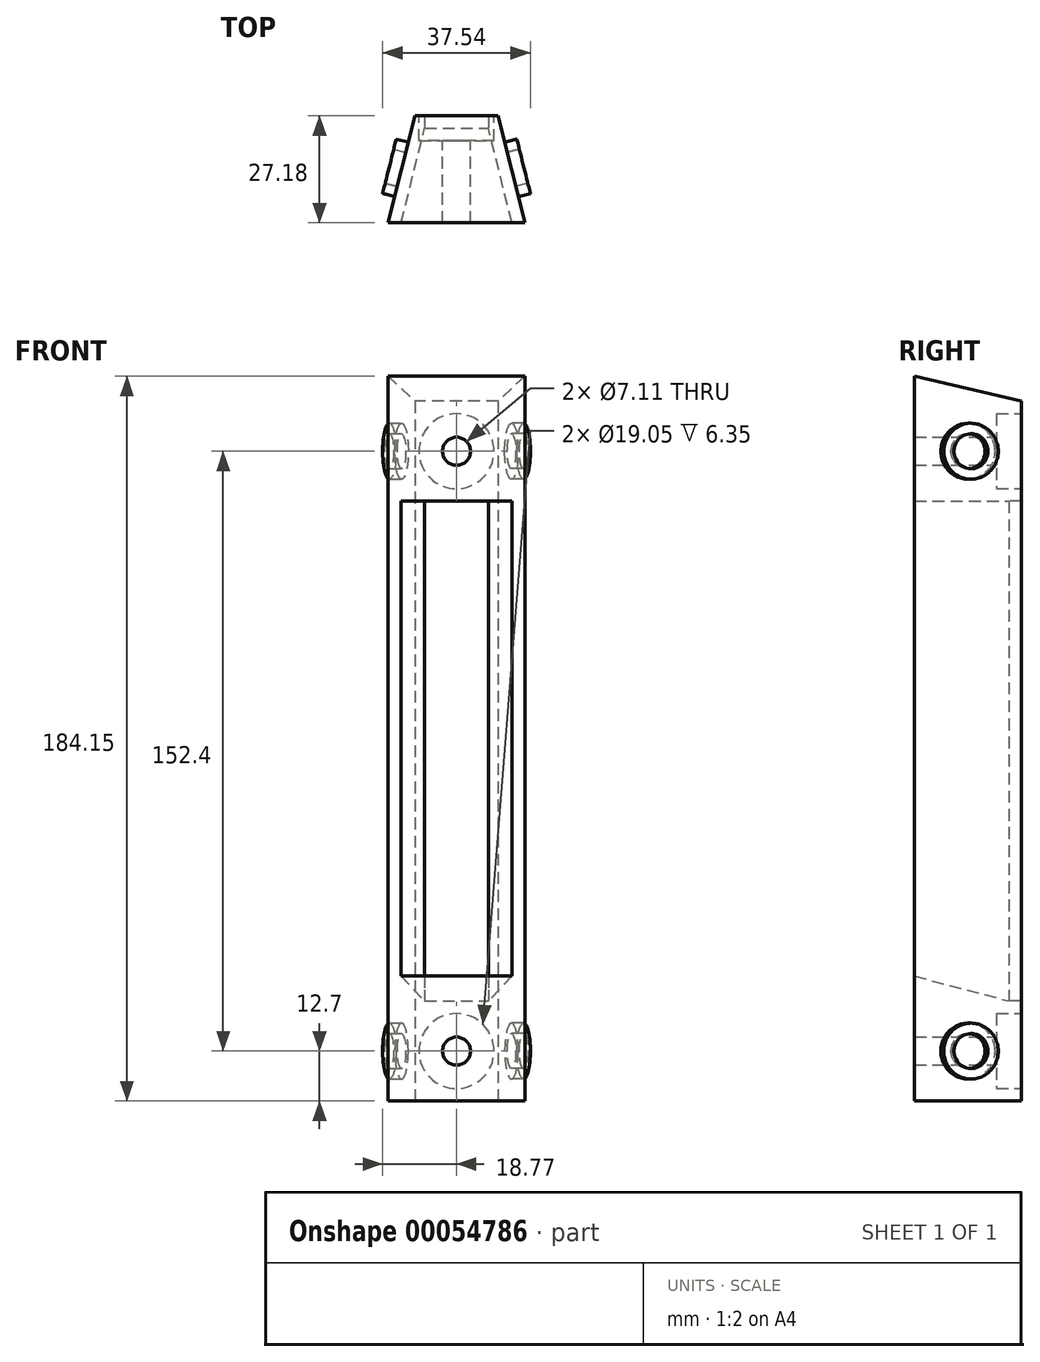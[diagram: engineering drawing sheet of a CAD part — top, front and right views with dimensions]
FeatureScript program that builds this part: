
annotation { "Feature Type Name" : "Feature", "Feature Type Description" : "" }
export const myFeature = defineFeature(function(context is Context, id is Id, definition is map)
    precondition{}
    {
        {
            var Q0;
            Q0=qCreatedBy(makeId("Top.planeOp"),FACE);
            var sketch = newSketch(context, id + "F0", { "sketchPlane" : qUnion([Q0])});
            skLineSegment(sketch, "E0", {"start": v(-39.69, 0) * mm, "end": v(-20.64, 0) * mm});
            skLineSegment(sketch, "E1", {"start": v(-20.64, 0) * mm, "end": v(-13.3, 29.35) * mm});
            skLineSegment(sketch, "E2", {"start": v(-10.22, 31.75) * mm, "end": v(10.22, 31.75) * mm});
            skLineSegment(sketch, "E3", {"start": v(13.3, 29.35) * mm, "end": v(20.64, 0) * mm});
            skLineSegment(sketch, "E4", {"start": v(20.64, 0) * mm, "end": v(39.69, 0) * mm});
            skLineSegment(sketch, "E5", {"start": v(0, 0) * mm, "end": v(0, 38.89) * mm, "construction": true});
            skPoint(sketch, "E6.visualSharp", {"position": v(-12.7, 31.75) * mm});
            skArc(sketch, "E6.filletArc", {"start": v(-10.22, 31.75) * mm, "mid": v(-12.17, 31.08) * mm, "end": v(-13.3, 29.35) * mm});
            skPoint(sketch, "E7.visualSharp", {"position": v(12.7, 31.75) * mm});
            skArc(sketch, "E7.filletArc", {"start": v(13.3, 29.35) * mm, "mid": v(12.17, 31.08) * mm, "end": v(10.22, 31.75) * mm});
            skLineSegment(sketch, "E8", {"start": v(-17.36, 0) * mm, "end": v(-14.1, 0) * mm});
            skLineSegment(sketch, "E9", {"start": v(-14.1, 0) * mm, "end": v(-8.1, 24) * mm});
            skLineSegment(sketch, "E10", {"start": v(-8.1, 24) * mm, "end": v(8.1, 24) * mm});
            skLineSegment(sketch, "E11", {"start": v(8.1, 24) * mm, "end": v(14.1, 0) * mm});
            skLineSegment(sketch, "E12", {"start": v(14.1, 0) * mm, "end": v(17.36, 0) * mm});
            skLineSegment(sketch, "E13", {"start": v(17.36, 0) * mm, "end": v(10.57, 27.18) * mm});
            skLineSegment(sketch, "E14", {"start": v(10.57, 27.18) * mm, "end": v(-10.57, 27.18) * mm});
            skLineSegment(sketch, "E15", {"start": v(-10.57, 27.18) * mm, "end": v(-17.36, 0) * mm});
            skSolve(sketch);
        }
        {
            var Q0;
            Q0=makeQuery(id+"F0.imprint","IMPRINT",FACE,{"disambiguationData":[TD([[makeQuery(id+"F0.imprint","IMPRINT",EDGE,{"derivedFrom":sQuery(id+"F0.wireOp",EDGE,"E8")}),1.0]])]});
            extrude(context, id + "F1", {"entities" : qUnion([Q0]), "depth" : 127 * mm});
        }
        {
            var Q0;
            Q0=makeQuery(id+"F1.opExtrude","CAP_FACE",FACE,{"disambiguationData":[OSD([sQuery(id+"F0.wireOp",EDGE,"E8"),sQuery(id+"F0.wireOp",EDGE,"E9"),sQuery(id+"F0.wireOp",EDGE,"E10"),sQuery(id+"F0.wireOp",EDGE,"E11"),sQuery(id+"F0.wireOp",EDGE,"E12"),sQuery(id+"F0.wireOp",EDGE,"E13"),sQuery(id+"F0.wireOp",EDGE,"E14"),sQuery(id+"F0.wireOp",EDGE,"E15")])],"isStart":true});
            var sketch = newSketch(context, id + "F2", { "sketchPlane" : qUnion([Q0])});
            skLineSegment(sketch, "E16", {"start": v(14.1, 0) * mm, "end": v(-14.1, 0) * mm});
            skSolve(sketch);
        }
        {
            var Q0;
            Q0=makeQuery(id+"F2.imprint","IMPRINT",FACE,{"disambiguationData":[TD([[makeQuery(id+"F2.imprint","IMPRINT",EDGE,{"derivedFrom":sQuery(id+"F2.wireOp",EDGE,"E16")}),1.0]])]});
            var Q1;
            Q1=makeQuery(id+"F2.imprint","IMPRINT",FACE,{"disambiguationData":[TD([[makeQuery(id+"F2.imprint","IMPRINT",EDGE,{"derivedFrom":makeQuery(id+"F1.opExtrude","CAP_EDGE",EDGE,{"disambiguationData":[OSD([sQuery(id+"F0.wireOp",EDGE,"E8")])],"isStart":true})}),-1.0]])]});
            extrude(context, id + "F3", {"entities" : qUnion([Q0, Q1]), "operationType" : NewBodyOperationType.ADD, "depth" : 25.4 * mm});
        }
        {
            var Q0;
            Q0=makeQuery(id+"F1.opExtrude","CAP_FACE",FACE,{"disambiguationData":[OSD([sQuery(id+"F0.wireOp",EDGE,"E8"),sQuery(id+"F0.wireOp",EDGE,"E9"),sQuery(id+"F0.wireOp",EDGE,"E10"),sQuery(id+"F0.wireOp",EDGE,"E11"),sQuery(id+"F0.wireOp",EDGE,"E12"),sQuery(id+"F0.wireOp",EDGE,"E13"),sQuery(id+"F0.wireOp",EDGE,"E14"),sQuery(id+"F0.wireOp",EDGE,"E15")])],"isStart":false});
            var sketch = newSketch(context, id + "F4", { "sketchPlane" : qUnion([Q0])});
            skLineSegment(sketch, "E17", {"start": v(-14.1, 0) * mm, "end": v(14.1, 0) * mm});
            skSolve(sketch);
        }
        {
            var Q0;
            Q0=makeQuery(id+"F4.imprint","IMPRINT",FACE,{"disambiguationData":[TD([[makeQuery(id+"F4.imprint","IMPRINT",EDGE,{"derivedFrom":sQuery(id+"F4.wireOp",EDGE,"E17")}),1.0]])]});
            var Q1;
            Q1=makeQuery(id+"F4.imprint","IMPRINT",FACE,{"disambiguationData":[TD([[makeQuery(id+"F4.imprint","IMPRINT",EDGE,{"derivedFrom":makeQuery(id+"F1.opExtrude","CAP_EDGE",EDGE,{"disambiguationData":[OSD([sQuery(id+"F0.wireOp",EDGE,"E8")])],"isStart":false})}),1.0]])]});
            extrude(context, id + "F5", {"entities" : qUnion([Q0, Q1]), "operationType" : NewBodyOperationType.ADD, "depth" : 25.4 * mm});
        }
        {
            var Q0;
            {var subQ0=sQuery(id+"F0.wireOp",EDGE,"E13");Q0=makeQuery(id+"F5.boolean.opBoolean","MERGE",FACE,{"derivedFrom":[makeQuery(id+"F3.boolean.opBoolean","MERGE",FACE,{"derivedFrom":[makeQuery(id+"F1.opExtrude","SWEPT_FACE",FACE,{"disambiguationData":[OSD([subQ0])]}),makeQuery(id+"F3.opExtrude","SWEPT_FACE",FACE,{"disambiguationData":[OSD([subQ0])]})]}),makeQuery(id+"F5.opExtrude","SWEPT_FACE",FACE,{"disambiguationData":[OSD([subQ0])]})]});}
            var sketch = newSketch(context, id + "F6", { "sketchPlane" : qUnion([Q0])});
            skLineSegment(sketch, "E18", {"start": v(-4.21, 152.4) * mm, "end": v(-4.21, 158.75) * mm});
            skLineSegment(sketch, "E19", {"start": v(-4.21, 158.75) * mm, "end": v(23.8, 152.4) * mm});
            skSolve(sketch);
        }
        {
            var Q0;
            {var subQ0=sQuery(id+"F0.wireOp",EDGE,"E15");Q0=makeQuery(id+"F5.boolean.opBoolean","MERGE",FACE,{"derivedFrom":[makeQuery(id+"F3.boolean.opBoolean","MERGE",FACE,{"derivedFrom":[makeQuery(id+"F1.opExtrude","SWEPT_FACE",FACE,{"disambiguationData":[OSD([subQ0])]}),makeQuery(id+"F3.opExtrude","SWEPT_FACE",FACE,{"disambiguationData":[OSD([subQ0])]})]}),makeQuery(id+"F5.opExtrude","SWEPT_FACE",FACE,{"disambiguationData":[OSD([subQ0])]})]});}
            var sketch = newSketch(context, id + "F7", { "sketchPlane" : qUnion([Q0])});
            skLineSegment(sketch, "E20", {"start": v(4.21, 152.4) * mm, "end": v(4.21, 158.75) * mm});
            skLineSegment(sketch, "E21", {"start": v(4.21, 158.75) * mm, "end": v(-23.8, 152.4) * mm});
            skSolve(sketch);
        }
        {
            var Q1;
            Q1=makeQuery(id+"F6.imprint","IMPRINT",FACE,{"disambiguationData":[TD([[makeQuery(id+"F6.imprint","IMPRINT",EDGE,{"derivedFrom":sQuery(id+"F6.wireOp",EDGE,"E18")}),-1.0]])]});
            var Q2;
            Q2=makeQuery(id+"F7.imprint","IMPRINT",FACE,{"disambiguationData":[TD([[makeQuery(id+"F7.imprint","IMPRINT",EDGE,{"derivedFrom":sQuery(id+"F7.wireOp",EDGE,"E20")}),1.0]])]});
            loft(context, id + "F8", {"operationType" : NewBodyOperationType.ADD, "sheetProfilesArray" : [{ "sheetProfileEntities" : qUnion([Q1]) }, { "sheetProfileEntities" : qUnion([Q2]) }]});
        }
        {
            var Q0;
            Q0=makeQuery(id+"F1.opExtrude","SWEPT_FACE",FACE,{"disambiguationData":[OSD([sQuery(id+"F0.wireOp",EDGE,"E11")])]});
            var sketch = newSketch(context, id + "F9", { "sketchPlane" : qUnion([Q0])});
            skLineSegment(sketch, "E22", {"start": v(3.42, 0) * mm, "end": v(3.42, 6.35) * mm});
            skLineSegment(sketch, "E23", {"start": v(3.42, 6.35) * mm, "end": v(-21.32, 0) * mm});
            skSolve(sketch);
        }
        {
            var Q0;
            Q0=makeQuery(id+"F1.opExtrude","SWEPT_FACE",FACE,{"disambiguationData":[OSD([sQuery(id+"F0.wireOp",EDGE,"E9")])]});
            var sketch = newSketch(context, id + "F10", { "sketchPlane" : qUnion([Q0])});
            skLineSegment(sketch, "E24", {"start": v(-3.42, 0) * mm, "end": v(-3.42, 6.35) * mm});
            skLineSegment(sketch, "E25", {"start": v(-3.42, 6.35) * mm, "end": v(21.32, 0) * mm});
            skSolve(sketch);
        }
        {
            var Q1;
            Q1=makeQuery(id+"F10.imprint","IMPRINT",FACE,{"disambiguationData":[TD([[makeQuery(id+"F10.imprint","IMPRINT",EDGE,{"derivedFrom":sQuery(id+"F10.wireOp",EDGE,"E24")}),1.0]])]});
            var Q2;
            Q2=makeQuery(id+"F9.imprint","IMPRINT",FACE,{"disambiguationData":[TD([[makeQuery(id+"F9.imprint","IMPRINT",EDGE,{"derivedFrom":sQuery(id+"F9.wireOp",EDGE,"E22")}),-1.0]])]});
            loft(context, id + "F11", {"operationType" : NewBodyOperationType.ADD, "sheetProfilesArray" : [{ "sheetProfileEntities" : qUnion([Q1]) }, { "sheetProfileEntities" : qUnion([Q2]) }]});
        }
        {
            var Q0;
            Q0=makeQuery(id+"F1.opExtrude","SWEPT_FACE",FACE,{"disambiguationData":[OSD([sQuery(id+"F0.wireOp",EDGE,"E10")])]});
            extrude(context, id + "F12", {"entities" : qUnion([Q0]), "operationType" : NewBodyOperationType.REMOVE, "endBound" : BoundingType.THROUGH_ALL, "oppositeDirection" : true, "depth" : 25.4 * mm});
        }
        {
            var Q0;
            {var subQ0=sQuery(id+"F0.wireOp",EDGE,"E14");Q0=makeQuery(id+"F5.boolean.opBoolean","MERGE",FACE,{"derivedFrom":[makeQuery(id+"F3.boolean.opBoolean","MERGE",FACE,{"derivedFrom":[makeQuery(id+"F1.opExtrude","SWEPT_FACE",FACE,{"disambiguationData":[OSD([subQ0])]}),makeQuery(id+"F3.opExtrude","SWEPT_FACE",FACE,{"disambiguationData":[OSD([subQ0])]})]}),makeQuery(id+"F5.opExtrude","SWEPT_FACE",FACE,{"disambiguationData":[OSD([subQ0])]})]});}
            var sketch = newSketch(context, id + "F13", { "sketchPlane" : qUnion([Q0])});
            skLineSegment(sketch, "E26", {"start": v(0, 152.4) * mm, "end": v(0, 139.7) * mm, "construction": true});
            skPoint(sketch, "E26.endSnap0", {"position": v(0, 152.4) * mm});
            skLineSegment(sketch, "E27", {"start": v(0, -25.4) * mm, "end": v(0, -12.7) * mm});
            skSolve(sketch);
        }
        {
            var Q0;
            Q0=sQuery(id+"F13.wireOp",VERTEX,"E26.end");
            var Q1;
            Q1=sQuery(id+"F13.wireOp",VERTEX,"E27.end");
            var Q2;
            Q2=makeQuery(id+"F1.opExtrude","SWEPT_BODY",BODY,{"disambiguationData":[OSD([sQuery(id+"F0.wireOp",EDGE,"E8"),sQuery(id+"F0.wireOp",EDGE,"E9"),sQuery(id+"F0.wireOp",EDGE,"E10"),sQuery(id+"F0.wireOp",EDGE,"E11"),sQuery(id+"F0.wireOp",EDGE,"E12"),sQuery(id+"F0.wireOp",EDGE,"E13"),sQuery(id+"F0.wireOp",EDGE,"E14"),sQuery(id+"F0.wireOp",EDGE,"E15")])]});
            hole(context, id + "F14", {"style" : HoleStyle.C_BORE, "holeDiameter" : 7.11 * mm, "cBoreDiameter" : 19.05 * mm, "cBoreDepth" : 6.35 * mm, "endStyle" : HoleEndStyle.THROUGH, "locations" : qUnion([Q0, Q1]), "scope" : qUnion([Q2])});
        }
        {
            var Q0;
            {var subQ0=sQuery(id+"F0.wireOp",EDGE,"E13");Q0=makeQuery(id+"F8.boolean.opBoolean","MERGE",FACE,{"derivedFrom":[makeQuery(id+"F5.boolean.opBoolean","MERGE",FACE,{"derivedFrom":[makeQuery(id+"F3.boolean.opBoolean","MERGE",FACE,{"derivedFrom":[makeQuery(id+"F1.opExtrude","SWEPT_FACE",FACE,{"disambiguationData":[OSD([subQ0])]}),makeQuery(id+"F3.opExtrude","SWEPT_FACE",FACE,{"disambiguationData":[OSD([subQ0])]})]}),makeQuery(id+"F5.opExtrude","SWEPT_FACE",FACE,{"disambiguationData":[OSD([subQ0])]})]}),makeQuery(id+"F8.opLoft","CAP_FACE",FACE,{"disambiguationData":[OSD([makeQuery(id+"F6.imprint","IMPRINT",FACE,{"disambiguationData":[TD([[makeQuery(id+"F6.imprint","IMPRINT",EDGE,{"derivedFrom":sQuery(id+"F6.wireOp",EDGE,"E18")}),-1.0]])]})])],"isStart":true})]});}
            var sketch = newSketch(context, id + "F15", { "sketchPlane" : qUnion([Q0])});
            skLineSegment(sketch, "E28", {"start": v(9.8, -25.4) * mm, "end": v(9.8, -12.7) * mm, "construction": true});
            skLineSegment(sketch, "E29", {"start": v(9.8, 155.58) * mm, "end": v(9.8, 139.7) * mm, "construction": true});
            skCircle(sketch, "E30", {"center": v(9.8, 139.7) * mm, "radius": 7.11 * mm});
            skCircle(sketch, "E31", {"center": v(9.8, 139.7) * mm, "radius": 4.45 * mm});
            skCircle(sketch, "E32", {"center": v(9.8, -12.7) * mm, "radius": 4.45 * mm});
            skCircle(sketch, "E33", {"center": v(9.8, -12.7) * mm, "radius": 7.11 * mm});
            skSolve(sketch);
        }
        {
            var Q0;
            Q0=makeQuery(id+"F15.imprint","IMPRINT",FACE,{"disambiguationData":[TD([[makeQuery(id+"F15.imprint","IMPRINT",EDGE,{"derivedFrom":sQuery(id+"F15.wireOp",EDGE,"E30")}),1.0]])]});
            var Q1;
            Q1=makeQuery(id+"F15.imprint","IMPRINT",FACE,{"disambiguationData":[TD([[makeQuery(id+"F15.imprint","IMPRINT",EDGE,{"derivedFrom":sQuery(id+"F15.wireOp",EDGE,"E32")}),-1.0]])]});
            extrude(context, id + "F16", {"entities" : qUnion([Q0, Q1]), "operationType" : NewBodyOperationType.ADD, "depth" : 3.17 * mm});
        }
        {
            var Q0;
            {var subQ0=sQuery(id+"F0.wireOp",EDGE,"E15");Q0=makeQuery(id+"F8.boolean.opBoolean","MERGE",FACE,{"derivedFrom":[makeQuery(id+"F5.boolean.opBoolean","MERGE",FACE,{"derivedFrom":[makeQuery(id+"F3.boolean.opBoolean","MERGE",FACE,{"derivedFrom":[makeQuery(id+"F1.opExtrude","SWEPT_FACE",FACE,{"disambiguationData":[OSD([subQ0])]}),makeQuery(id+"F3.opExtrude","SWEPT_FACE",FACE,{"disambiguationData":[OSD([subQ0])]})]}),makeQuery(id+"F5.opExtrude","SWEPT_FACE",FACE,{"disambiguationData":[OSD([subQ0])]})]}),makeQuery(id+"F8.opLoft","CAP_FACE",FACE,{"disambiguationData":[OSD([makeQuery(id+"F7.imprint","IMPRINT",FACE,{"disambiguationData":[TD([[makeQuery(id+"F7.imprint","IMPRINT",EDGE,{"derivedFrom":sQuery(id+"F7.wireOp",EDGE,"E20")}),1.0]])]})])],"isStart":true})]});}
            var sketch = newSketch(context, id + "F17", { "sketchPlane" : qUnion([Q0])});
            skLineSegment(sketch, "E34", {"start": v(-9.8, 155.57) * mm, "end": v(-9.8, 139.7) * mm, "construction": true});
            skLineSegment(sketch, "E35", {"start": v(-9.8, -25.4) * mm, "end": v(-9.8, -12.7) * mm, "construction": true});
            skCircle(sketch, "E36", {"center": v(-9.8, 139.7) * mm, "radius": 4.45 * mm});
            skCircle(sketch, "E37", {"center": v(-9.8, 139.7) * mm, "radius": 7.11 * mm});
            skCircle(sketch, "E38", {"center": v(-9.8, -12.7) * mm, "radius": 4.45 * mm});
            skCircle(sketch, "E39", {"center": v(-9.8, -12.7) * mm, "radius": 7.11 * mm});
            skSolve(sketch);
        }
        {
            var Q0;
            Q0=makeQuery(id+"F17.imprint","IMPRINT",FACE,{"disambiguationData":[TD([[makeQuery(id+"F17.imprint","IMPRINT",EDGE,{"derivedFrom":sQuery(id+"F17.wireOp",EDGE,"E36")}),-1.0]])]});
            var Q1;
            Q1=makeQuery(id+"F17.imprint","IMPRINT",FACE,{"disambiguationData":[TD([[makeQuery(id+"F17.imprint","IMPRINT",EDGE,{"derivedFrom":sQuery(id+"F17.wireOp",EDGE,"E38")}),-1.0]])]});
            extrude(context, id + "F18", {"entities" : qUnion([Q0, Q1]), "operationType" : NewBodyOperationType.ADD, "depth" : 3.17 * mm});
        }
    });
